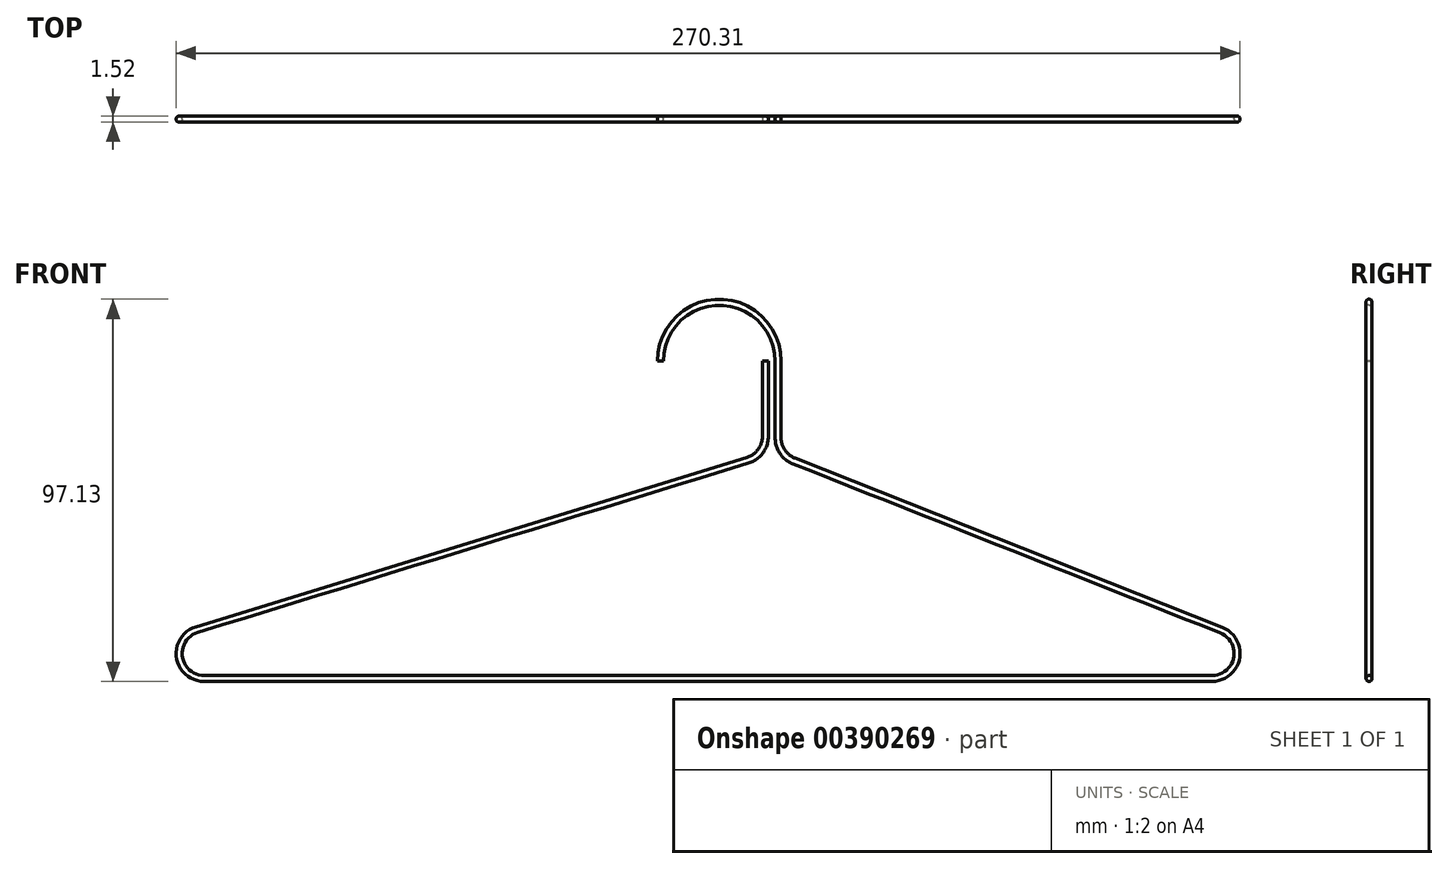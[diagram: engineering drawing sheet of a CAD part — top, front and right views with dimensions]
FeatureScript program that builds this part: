
annotation { "Feature Type Name" : "Feature", "Feature Type Description" : "" }
export const myFeature = defineFeature(function(context is Context, id is Id, definition is map)
    precondition{}
    {
        {
            var Q0;
            Q0=qCreatedBy(makeId("Front.planeOp"),FACE);
            var sketch = newSketch(context, id + "F0", { "sketchPlane" : qUnion([Q0])});
            skLineSegment(sketch, "E0", {"start": v(39.5, 0) * mm, "end": v(39.5, -19.12) * mm});
            skLineSegment(sketch, "E1", {"start": v(35.03, -25.2) * mm, "end": v(-104.95, -68.23) * mm});
            skLineSegment(sketch, "E2", {"start": v(-103.08, -80.65) * mm, "end": v(153, -80.65) * mm});
            skLineSegment(sketch, "E3", {"start": v(155.34, -68.4) * mm, "end": v(46.75, -25.4) * mm});
            skLineSegment(sketch, "E4", {"start": v(42.74, -19.5) * mm, "end": v(42.74, 0) * mm});
            skArc(sketch, "E5", {"start": v(42.74, 0) * mm, "mid": v(27.79, 14.95) * mm, "end": v(12.83, 0) * mm});
            skPoint(sketch, "E6.visualSharp", {"position": v(42.74, -23.81) * mm});
            skArc(sketch, "E6.filletArc", {"start": v(42.74, -19.5) * mm, "mid": v(43.84, -23.07) * mm, "end": v(46.75, -25.4) * mm});
            skPoint(sketch, "E7.visualSharp", {"position": v(39.5, -23.81) * mm});
            skArc(sketch, "E7.filletArc", {"start": v(35.03, -25.2) * mm, "mid": v(38.27, -22.9) * mm, "end": v(39.5, -19.12) * mm});
            skPoint(sketch, "E8.visualSharp", {"position": v(186.3, -80.65) * mm});
            skArc(sketch, "E8.filletArc", {"start": v(153, -80.65) * mm, "mid": v(159.24, -75.49) * mm, "end": v(155.34, -68.4) * mm});
            skPoint(sketch, "E9.visualSharp", {"position": v(-145.34, -80.65) * mm});
            skArc(sketch, "E9.filletArc", {"start": v(-104.95, -68.23) * mm, "mid": v(-109.36, -75.24) * mm, "end": v(-103.08, -80.65) * mm});
            skSolve(sketch);
        }
        {
            var Q0;
            Q0=qCreatedBy(makeId("Top.planeOp"),FACE);
            var sketch = newSketch(context, id + "F1", { "sketchPlane" : qUnion([Q0])});
            skCircle(sketch, "E10", {"center": v(12.83, 0) * mm, "radius": 0.76 * mm});
            skSolve(sketch);
        }
        {
            var Q0;
            Q0=makeQuery(id+"F1.imprint","IMPRINT",FACE,{"disambiguationData":[TD([[makeQuery(id+"F1.imprint","IMPRINT",EDGE,{"derivedFrom":sQuery(id+"F1.wireOp",EDGE,"E10")}),1.0]])]});
            var Q1;
            Q1=sQuery(id+"F0.wireOp",EDGE,"E5");
            var Q2;
            Q2=sQuery(id+"F0.wireOp",EDGE,"E4");
            var Q3;
            Q3=sQuery(id+"F0.wireOp",EDGE,"E6.filletArc");
            var Q4;
            Q4=sQuery(id+"F0.wireOp",EDGE,"E3");
            var Q5;
            Q5=sQuery(id+"F0.wireOp",EDGE,"E8.filletArc");
            var Q6;
            Q6=sQuery(id+"F0.wireOp",EDGE,"E2");
            var Q7;
            Q7=sQuery(id+"F0.wireOp",EDGE,"E9.filletArc");
            var Q8;
            Q8=sQuery(id+"F0.wireOp",EDGE,"E1");
            var Q9;
            Q9=sQuery(id+"F0.wireOp",EDGE,"E7.filletArc");
            var Q10;
            Q10=sQuery(id+"F0.wireOp",EDGE,"E0");
            sweep(context, id + "F2", {"profiles" : qUnion([Q0]), "path" : qUnion([Q1, Q2, Q3, Q4, Q5, Q6, Q7, Q8, Q9, Q10])});
        }
    });
